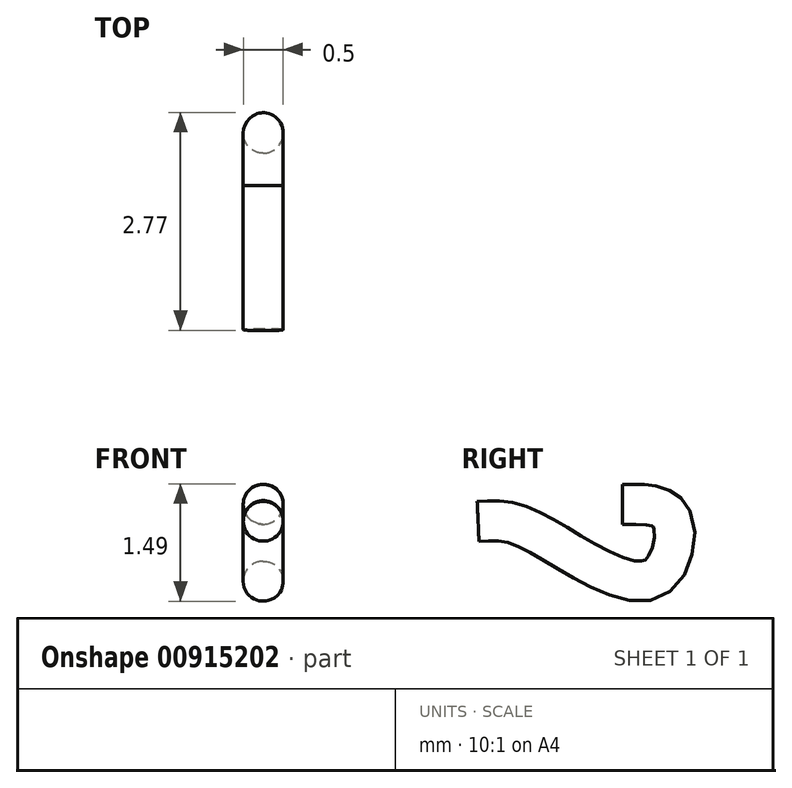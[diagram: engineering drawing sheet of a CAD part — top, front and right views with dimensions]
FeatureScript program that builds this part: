
annotation { "Feature Type Name" : "Feature", "Feature Type Description" : "" }
export const myFeature = defineFeature(function(context is Context, id is Id, definition is map)
    precondition{}
    {
        {
            var Q0;
            Q0=qCreatedBy(makeId("Front.planeOp"),FACE);
            var sketch = newSketch(context, id + "F0", { "sketchPlane" : qUnion([Q0])});
            skCircle(sketch, "E0", {"center": v(0, 0) * mm, "radius": 0.25 * mm});
            skSolve(sketch);
        }
        {
            var Q0;
            Q0=qCreatedBy(makeId("Right.planeOp"),FACE);
            var sketch = newSketch(context, id + "F1", { "sketchPlane" : qUnion([Q0])});
            skFitSpline(sketch, "E1", {"points": [v(0, 0) * mm, v(0.62, -0.17) * mm, v(0.44, -0.91) * mm, v(-0.48, -0.72) * mm, v(-1.36, -0.25) * mm, v(-1.83, -0.21) * mm], "startDerivative": vector(4.22, 0.09) * mm, "endDerivative": vector(-2.84, -0.18) * mm});
            skSolve(sketch);
        }
        {
            var Q0;
            Q0=makeQuery(id+"F0.imprint","IMPRINT",FACE,{"disambiguationData":[TD([[makeQuery(id+"F0.imprint","IMPRINT",EDGE,{"derivedFrom":sQuery(id+"F0.wireOp",EDGE,"E0")}),1.0]])]});
            var Q1;
            Q1=sQuery(id+"F1.wireOp",EDGE,"E1");
            sweep(context, id + "F2", {"profiles" : qUnion([Q0]), "path" : qUnion([Q1])});
        }
    });
